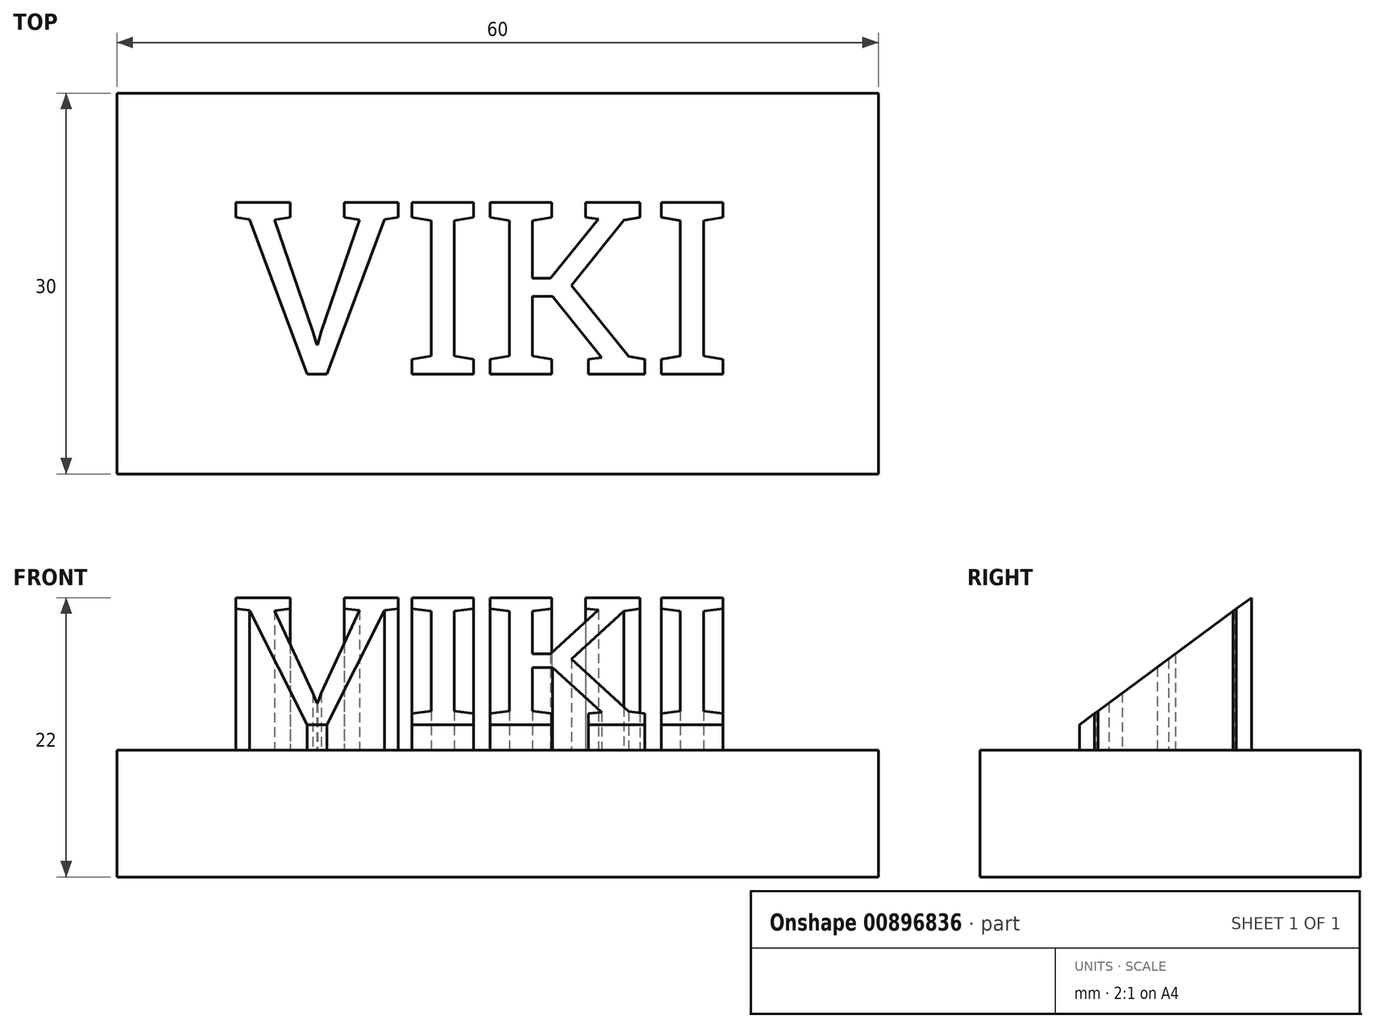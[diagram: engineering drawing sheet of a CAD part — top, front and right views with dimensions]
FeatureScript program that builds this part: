
annotation { "Feature Type Name" : "Feature", "Feature Type Description" : "" }
export const myFeature = defineFeature(function(context is Context, id is Id, definition is map)
    precondition{}
    {
        {
            var Q0;
            Q0=qCreatedBy(makeId("Top.planeOp"),FACE);
            var sketch = newSketch(context, id + "F0", { "sketchPlane" : qUnion([Q0])});
            skLineSegment(sketch, "E0.bottom", {"start": v(31.66, -15) * mm, "end": v(-28.34, -15) * mm});
            skLineSegment(sketch, "E0.top", {"start": v(31.66, 15) * mm, "end": v(-28.34, 15) * mm});
            skLineSegment(sketch, "E0.left", {"start": v(31.66, -15) * mm, "end": v(31.66, 15) * mm});
            skLineSegment(sketch, "E0.right", {"start": v(-28.34, -15) * mm, "end": v(-28.34, 15) * mm});
            skPoint(sketch, "E0.middle", {"position": v(1.66, 0) * mm});
            skSolve(sketch);
        }
        {
            var Q0;
            Q0=makeQuery(id+"F0.imprint","IMPRINT",FACE,{"disambiguationData":[TD([[makeQuery(id+"F0.imprint","IMPRINT",EDGE,{"derivedFrom":sQuery(id+"F0.wireOp",EDGE,"E0.bottom")}),-1.0]])]});
            extrude(context, id + "F1", {"entities" : qUnion([Q0]), "flatOperationType" : FlatOperationType.REMOVE, "depth" : 10 * mm, "offsetDistance" : 25 * mm, "domain" : OperationDomain.MODEL});
        }
        {
            var Q0;
            Q0=makeQuery(id+"F1.opExtrude","CAP_FACE",FACE,{"disambiguationData":[OSD([sQuery(id+"F0.wireOp",EDGE,"E0.bottom"),sQuery(id+"F0.wireOp",EDGE,"E0.top"),sQuery(id+"F0.wireOp",EDGE,"E0.left"),sQuery(id+"F0.wireOp",EDGE,"E0.right")])],"isStart":false});
            var sketch = newSketch(context, id + "F2", { "sketchPlane" : qUnion([Q0])});
            skLineSegment(sketch, "E1.0.0", {"start": v(31.66, -15) * mm, "end": v(31.66, 15) * mm});
            skLineSegment(sketch, "E1.0.1", {"start": v(31.66, 15) * mm, "end": v(-28.34, 15) * mm});
            skLineSegment(sketch, "E1.0.2", {"start": v(-28.34, 15) * mm, "end": v(-28.34, -15) * mm});
            skLineSegment(sketch, "E1.0.3", {"start": v(-28.34, -15) * mm, "end": v(31.66, -15) * mm});
            skLineSegment(sketch, "E2", {"start": v(-28.34, 12) * mm, "end": v(31.66, 12) * mm});
            skLineSegment(sketch, "E3", {"start": v(-28.34, -12) * mm, "end": v(31.66, -12) * mm});
            skPoint(sketch, "E3.startSnap0", {"position": v(-14.7, -12) * mm});
            skLineSegment(sketch, "E4", {"start": v(-26.34, -15) * mm, "end": v(-26.34, 15) * mm});
            skLineSegment(sketch, "E5", {"start": v(29.66, 15) * mm, "end": v(29.66, -15) * mm});
            skText(sketch, "E6", { "text": "VIKI", "fontName": "RobotoSlab-Regular.ttf"});
            const initialGuessF2  = {"E6": [-0.0194, -0.00713, 1, 0, 0.0137]};
            skSetInitialGuess(sketch, initialGuessF2);
            skSolve(sketch);
        }
        {
            var Q0;
            Q0=makeQuery(id+"F2.imprint","IMPRINT",FACE,{"disambiguationData":[TD([[makeQuery(id+"F2.imprint","IMPRINT",EDGE,{"derivedFrom":sQuery(id+"F2.wireOp",EDGE,"E6.sketch_text.stroke-0")}),-1.0]])]});
            var Q1;
            Q1=makeQuery(id+"F2.imprint","IMPRINT",FACE,{"disambiguationData":[TD([[makeQuery(id+"F2.imprint","IMPRINT",EDGE,{"derivedFrom":sQuery(id+"F2.wireOp",EDGE,"E6.sketch_text.stroke-18")}),-1.0]])]});
            var Q2;
            Q2=makeQuery(id+"F2.imprint","IMPRINT",FACE,{"disambiguationData":[TD([[makeQuery(id+"F2.imprint","IMPRINT",EDGE,{"derivedFrom":sQuery(id+"F2.wireOp",EDGE,"E6.sketch_text.stroke-30")}),-1.0]])]});
            var Q3;
            Q3=makeQuery(id+"F2.imprint","IMPRINT",FACE,{"disambiguationData":[TD([[makeQuery(id+"F2.imprint","IMPRINT",EDGE,{"derivedFrom":sQuery(id+"F2.wireOp",EDGE,"E6.sketch_text.stroke-59")}),-1.0]])]});
            extrude(context, id + "F3", {"entities" : qUnion([Q0, Q1, Q2, Q3]), "operationType" : NewBodyOperationType.ADD, "flatOperationType" : FlatOperationType.REMOVE, "depth" : 12 * mm, "offsetDistance" : 25 * mm, "domain" : OperationDomain.MODEL});
        }
        {
            var Q0;
            Q0=makeQuery(id+"F3.opExtrude","SWEPT_FACE",FACE,{"disambiguationData":[OSD([sQuery(id+"F2.wireOp",EDGE,"E6.sketch_text.stroke-15")])]});
            var sketch = newSketch(context, id + "F4", { "sketchPlane" : qUnion([Q0])});
            skLineSegment(sketch, "E7.0", {"start": v(7.13, 22) * mm, "end": v(7.13, 10) * mm});
            skLineSegment(sketch, "E8.0", {"start": v(-6.4, 22) * mm, "end": v(-6.4, 10) * mm});
            skLineSegment(sketch, "E9", {"start": v(7.13, 10) * mm, "end": v(7.13, 12) * mm});
            skLineSegment(sketch, "E10", {"start": v(7.13, 12) * mm, "end": v(-6.4, 22) * mm});
            skLineSegment(sketch, "E11", {"start": v(7.13, 22) * mm, "end": v(-6.4, 22) * mm});
            skSolve(sketch);
        }
        {
            var Q0;
            {var subQ0=sQuery(id+"F4.wireOp",EDGE,"E11");var subQ1=sQuery(id+"F4.wireOp",EDGE,"E7.0");var subQ2=makeQuery(id+"F4.imprint","INTERSECT",VERTEX,{"derivedFrom":[subQ1,subQ0]});Q0=makeQuery(id+"F4.imprint","IMPRINT",FACE,{"disambiguationData":[TD([[makeQuery(id+"F4.imprint","IMPRINT",EDGE,{"disambiguationData":[TD([[subQ2,-1.0]])],"derivedFrom":subQ1}),-1.0]])]});}
            var Q1;
            {var subQ0=sQuery(id+"F4.wireOp",EDGE,"E11");var subQ1=sQuery(id+"F4.wireOp",EDGE,"E10");var subQ2=makeQuery(id+"F4.imprint","INTERSECT",VERTEX,{"derivedFrom":[sQuery(id+"F4.wireOp",EDGE,"E8.0"),subQ1,subQ0]});Q1=makeQuery(id+"F4.imprint","IMPRINT",FACE,{"disambiguationData":[TD([[makeQuery(id+"F4.imprint","IMPRINT",EDGE,{"disambiguationData":[TD([[subQ2,1.0]])],"derivedFrom":subQ1}),-1.0]])]});}
            extrude(context, id + "F5", {"entities" : qUnion([Q0, Q1]), "operationType" : NewBodyOperationType.REMOVE, "oppositeDirection" : true, "depth" : 50 * mm, "offsetDistance" : 25 * mm});
        }
    });
